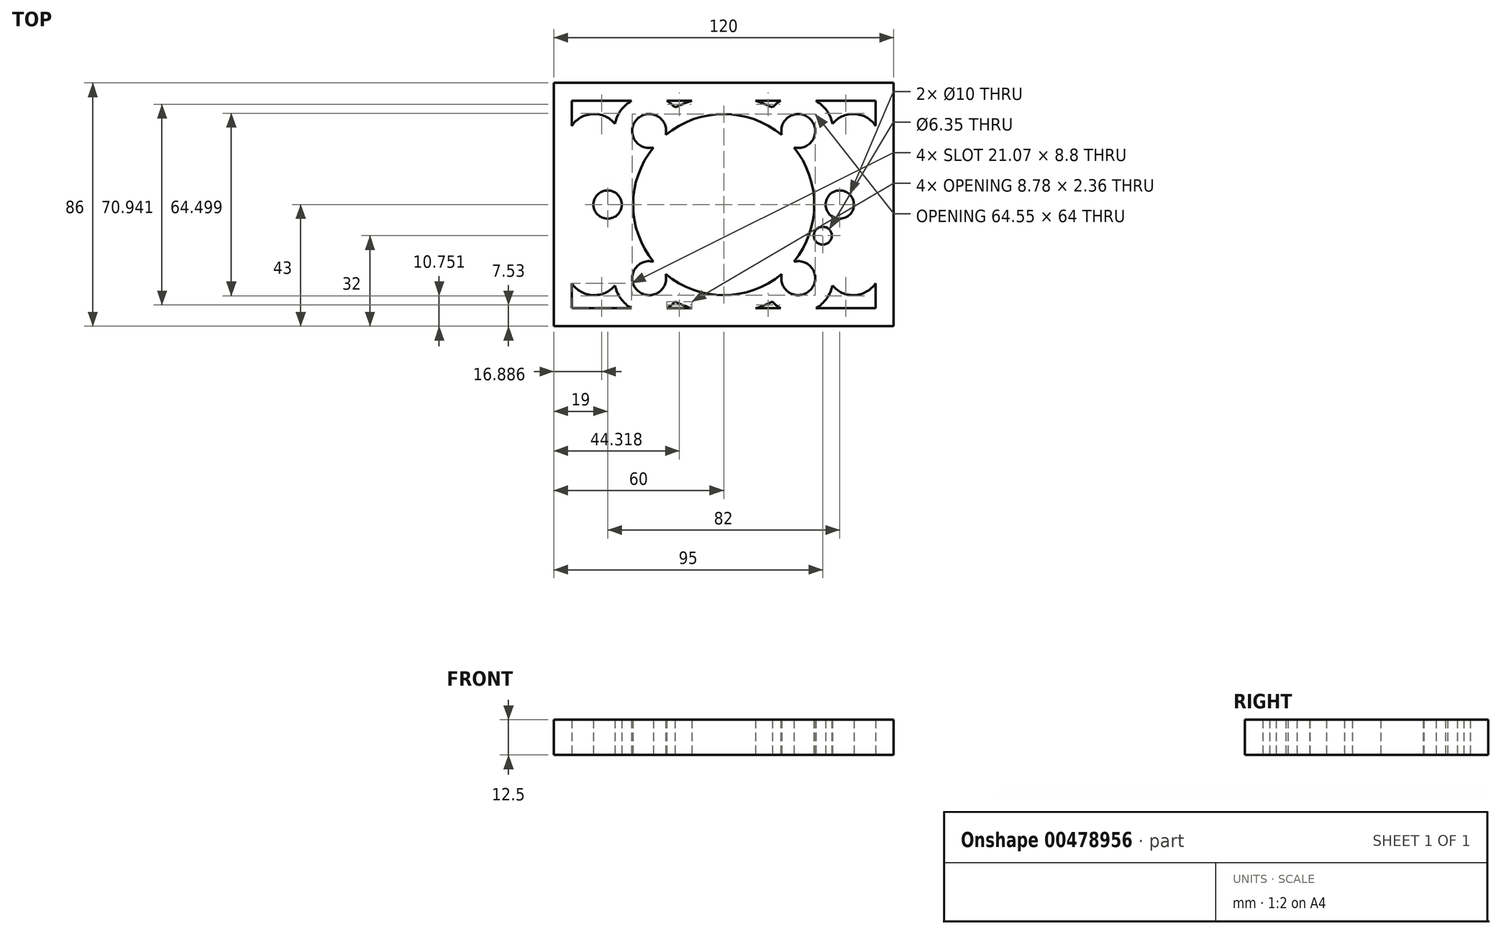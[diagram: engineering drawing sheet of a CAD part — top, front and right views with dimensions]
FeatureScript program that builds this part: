
annotation { "Feature Type Name" : "Feature", "Feature Type Description" : "" }
export const myFeature = defineFeature(function(context is Context, id is Id, definition is map)
    precondition{}
    {
        {
            var Q0;
            Q0=qCreatedBy(makeId("Top.planeOp"),FACE);
            var sketch = newSketch(context, id + "F0", { "sketchPlane" : qUnion([Q0])});
            skLineSegment(sketch, "E0", {"start": v(0, 60) * mm, "end": v(0, -60) * mm});
            skLineSegment(sketch, "E1", {"start": v(-70, 0) * mm, "end": v(70, 0) * mm});
            skLineSegment(sketch, "E2", {"start": v(-60, 43) * mm, "end": v(60, 43) * mm});
            skLineSegment(sketch, "E3", {"start": v(-60, -43) * mm, "end": v(60, -43) * mm});
            skCircle(sketch, "E4", {"center": v(-45.77, 22.5) * mm, "radius": 3.17 * mm});
            skCircle(sketch, "E5", {"center": v(-45.77, -22.5) * mm, "radius": 3.17 * mm});
            skCircle(sketch, "E6", {"center": v(45.77, -22.5) * mm, "radius": 3.17 * mm});
            skCircle(sketch, "E7", {"center": v(45.77, 22.5) * mm, "radius": 3.17 * mm});
            skCircle(sketch, "E8", {"center": v(-41, 0) * mm, "radius": 2.58 * mm});
            skCircle(sketch, "E9", {"center": v(41, 0) * mm, "radius": 2.58 * mm});
            skCircle(sketch, "E10", {"center": v(-41, 0) * mm, "radius": 5 * mm});
            skCircle(sketch, "E11", {"center": v(41, 0) * mm, "radius": 5 * mm});
            skLineSegment(sketch, "E12", {"start": v(60, 43) * mm, "end": v(60, -43) * mm});
            skLineSegment(sketch, "E13", {"start": v(-60, 43) * mm, "end": v(-60, -43) * mm});
            skArc(sketch, "E14", {"start": v(-24.83, 20.2) * mm, "mid": v(-32, 0) * mm, "end": v(-24.83, -20.2) * mm});
            skArc(sketch, "E15", {"start": v(-20.5, 24.57) * mm, "mid": v(-30.6, 30.22) * mm, "end": v(-24.83, 20.2) * mm});
            skArc(sketch, "E16", {"start": v(24.83, 20.2) * mm, "mid": v(30.6, 30.22) * mm, "end": v(20.5, 24.57) * mm});
            skArc(sketch, "E17", {"start": v(20.5, -24.57) * mm, "mid": v(30.6, -30.22) * mm, "end": v(24.83, -20.2) * mm});
            skArc(sketch, "E18", {"start": v(-24.83, -20.2) * mm, "mid": v(-30.6, -30.22) * mm, "end": v(-20.5, -24.57) * mm});
            skArc(sketch, "E19", {"start": v(20.5, 24.57) * mm, "mid": v(0, 32) * mm, "end": v(-20.5, 24.57) * mm});
            skArc(sketch, "E20", {"start": v(-20.5, -24.57) * mm, "mid": v(0, -32) * mm, "end": v(20.5, -24.57) * mm});
            skArc(sketch, "E21", {"start": v(24.83, -20.2) * mm, "mid": v(32, 0) * mm, "end": v(24.83, 20.2) * mm});
            skCircle(sketch, "E22", {"center": v(35, -11) * mm, "radius": 3.17 * mm});
            skLineSegment(sketch, "E23", {"start": v(-53.65, 36.65) * mm, "end": v(-53.65, 27.85) * mm});
            skLineSegment(sketch, "E24", {"start": v(-53.65, -36.65) * mm, "end": v(-32.58, -36.65) * mm});
            skLineSegment(sketch, "E25", {"start": v(53.65, 36.65) * mm, "end": v(53.65, 27.85) * mm});
            skArc(sketch, "E26", {"start": v(-17.17, -34.3) * mm, "mid": v(-14.28, -35.6) * mm, "end": v(-11.3, -36.65) * mm});
            skArc(sketch, "E27", {"start": v(17.17, 34.3) * mm, "mid": v(14.28, 35.6) * mm, "end": v(11.3, 36.65) * mm});
            skArc(sketch, "E28", {"start": v(53.65, 27.85) * mm, "mid": v(46.2, 32.02) * mm, "end": v(38.4, 28.55) * mm});
            skArc(sketch, "E29", {"start": v(38.4, -28.55) * mm, "mid": v(46.2, -32.02) * mm, "end": v(53.65, -27.85) * mm});
            skArc(sketch, "E30", {"start": v(17.17, -34.3) * mm, "mid": v(18.53, -35.58) * mm, "end": v(20.07, -36.65) * mm});
            skArc(sketch, "E31", {"start": v(-17.17, 34.3) * mm, "mid": v(-18.53, 35.58) * mm, "end": v(-20.07, 36.65) * mm});
            skLineSegment(sketch, "E32", {"start": v(-53.65, 36.65) * mm, "end": v(-32.58, 36.65) * mm});
            skLineSegment(sketch, "E33", {"start": v(-20.07, -36.65) * mm, "end": v(-11.3, -36.65) * mm});
            skArc(sketch, "E34", {"start": v(-38.4, -28.55) * mm, "mid": v(-36.35, -33.21) * mm, "end": v(-32.58, -36.65) * mm});
            skArc(sketch, "E35", {"start": v(-20.07, -36.65) * mm, "mid": v(-18.53, -35.58) * mm, "end": v(-17.17, -34.3) * mm});
            skArc(sketch, "E36", {"start": v(32.58, -36.65) * mm, "mid": v(36.35, -33.21) * mm, "end": v(38.4, -28.55) * mm});
            skArc(sketch, "E37", {"start": v(11.3, -36.65) * mm, "mid": v(14.28, -35.6) * mm, "end": v(17.17, -34.3) * mm});
            skLineSegment(sketch, "E38", {"start": v(11.3, -36.65) * mm, "end": v(20.07, -36.65) * mm});
            skLineSegment(sketch, "E39", {"start": v(-53.65, -27.85) * mm, "end": v(-53.65, -36.65) * mm});
            skArc(sketch, "E40", {"start": v(-53.65, -27.85) * mm, "mid": v(-46.2, -32.02) * mm, "end": v(-38.4, -28.55) * mm});
            skLineSegment(sketch, "E41", {"start": v(32.58, -36.65) * mm, "end": v(53.65, -36.65) * mm});
            skLineSegment(sketch, "E42", {"start": v(53.65, -27.85) * mm, "end": v(53.65, -36.65) * mm});
            skArc(sketch, "E43", {"start": v(-32.58, 36.65) * mm, "mid": v(-36.35, 33.21) * mm, "end": v(-38.4, 28.55) * mm});
            skArc(sketch, "E44", {"start": v(20.07, 36.65) * mm, "mid": v(18.53, 35.58) * mm, "end": v(17.17, 34.3) * mm});
            skLineSegment(sketch, "E45", {"start": v(11.3, 36.65) * mm, "end": v(20.07, 36.65) * mm});
            skLineSegment(sketch, "E46", {"start": v(-20.07, 36.65) * mm, "end": v(-11.3, 36.65) * mm});
            skLineSegment(sketch, "E47", {"start": v(32.58, 36.65) * mm, "end": v(53.65, 36.65) * mm});
            skArc(sketch, "E48", {"start": v(-38.4, 28.55) * mm, "mid": v(-46.2, 32.02) * mm, "end": v(-53.65, 27.85) * mm});
            skArc(sketch, "E49", {"start": v(38.4, 28.55) * mm, "mid": v(36.35, 33.21) * mm, "end": v(32.58, 36.65) * mm});
            skArc(sketch, "E50", {"start": v(-11.3, 36.65) * mm, "mid": v(-14.28, 35.6) * mm, "end": v(-17.17, 34.3) * mm});
            skSolve(sketch);
        }
        {
            var Q0;
            Q0=makeQuery(id+"F0.imprint","IMPRINT",FACE,{"disambiguationData":[TD([[makeQuery(id+"F0.imprint","IMPRINT",EDGE,{"derivedFrom":sQuery(id+"F0.wireOp",EDGE,"E4")}),1.0]])]});
            var Q1;
            {var subQ0=sQuery(id+"F0.wireOp",EDGE,"E11");var subQ1=sQuery(id+"F0.wireOp",EDGE,"E1");var subQ2=makeQuery(id+"F0.imprint","INTERSECT",VERTEX,{"disambiguationData":[OD(0.0)],"derivedFrom":[subQ1,subQ0]});Q1=makeQuery(id+"F0.imprint","IMPRINT",FACE,{"disambiguationData":[TD([[makeQuery(id+"F0.imprint","IMPRINT",EDGE,{"disambiguationData":[TD([[subQ2,-1.0]])],"derivedFrom":subQ1}),1.0]])]});}
            var Q2;
            {var subQ0=sQuery(id+"F0.wireOp",EDGE,"E11");var subQ1=sQuery(id+"F0.wireOp",EDGE,"E1");var subQ2=makeQuery(id+"F0.imprint","INTERSECT",VERTEX,{"disambiguationData":[OD(0.0)],"derivedFrom":[subQ1,subQ0]});Q2=makeQuery(id+"F0.imprint","IMPRINT",FACE,{"disambiguationData":[TD([[makeQuery(id+"F0.imprint","IMPRINT",EDGE,{"disambiguationData":[TD([[subQ2,-1.0]])],"derivedFrom":subQ1}),-1.0]])]});}
            var Q3;
            {var subQ0=sQuery(id+"F0.wireOp",EDGE,"E10");var subQ1=sQuery(id+"F0.wireOp",EDGE,"E1");var subQ2=makeQuery(id+"F0.imprint","INTERSECT",VERTEX,{"disambiguationData":[OD(0.0)],"derivedFrom":[subQ1,subQ0]});Q3=makeQuery(id+"F0.imprint","IMPRINT",FACE,{"disambiguationData":[TD([[makeQuery(id+"F0.imprint","IMPRINT",EDGE,{"disambiguationData":[TD([[subQ2,-1.0]])],"derivedFrom":subQ1}),-1.0]])]});}
            var Q4;
            {var subQ0=sQuery(id+"F0.wireOp",EDGE,"E10");var subQ1=sQuery(id+"F0.wireOp",EDGE,"E1");var subQ2=makeQuery(id+"F0.imprint","INTERSECT",VERTEX,{"disambiguationData":[OD(0.0)],"derivedFrom":[subQ1,subQ0]});Q4=makeQuery(id+"F0.imprint","IMPRINT",FACE,{"disambiguationData":[TD([[makeQuery(id+"F0.imprint","IMPRINT",EDGE,{"disambiguationData":[TD([[subQ2,-1.0]])],"derivedFrom":subQ1}),1.0]])]});}
            var Q5;
            Q5=makeQuery(id+"F0.imprint","IMPRINT",FACE,{"disambiguationData":[TD([[makeQuery(id+"F0.imprint","IMPRINT",EDGE,{"derivedFrom":sQuery(id+"F0.wireOp",EDGE,"E5")}),1.0]])]});
            var Q6;
            Q6=makeQuery(id+"F0.imprint","IMPRINT",FACE,{"disambiguationData":[TD([[makeQuery(id+"F0.imprint","IMPRINT",EDGE,{"derivedFrom":sQuery(id+"F0.wireOp",EDGE,"E7")}),1.0]])]});
            var Q7;
            Q7=makeQuery(id+"F0.imprint","IMPRINT",FACE,{"disambiguationData":[TD([[makeQuery(id+"F0.imprint","IMPRINT",EDGE,{"derivedFrom":sQuery(id+"F0.wireOp",EDGE,"E6")}),1.0]])]});
            extrude(context, id + "F1", {"entities" : qUnion([Q0, Q1, Q2, Q3, Q4, Q5, Q6, Q7]), "depth" : 12.5 * mm});
        }
    });
